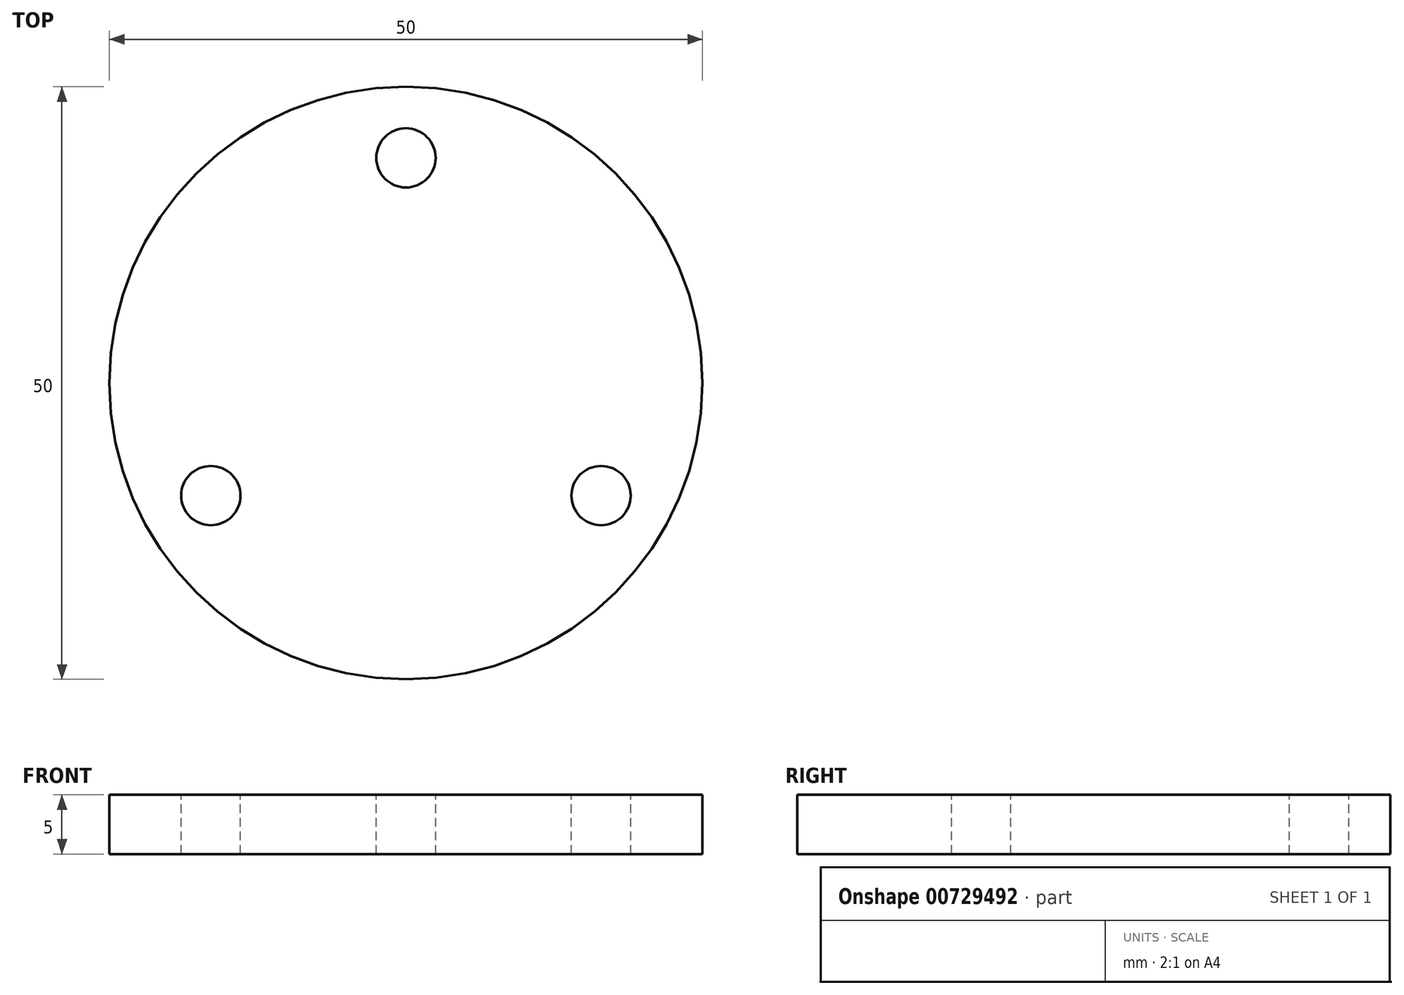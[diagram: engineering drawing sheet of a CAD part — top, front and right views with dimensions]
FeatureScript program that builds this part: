
annotation { "Feature Type Name" : "Feature", "Feature Type Description" : "" }
export const myFeature = defineFeature(function(context is Context, id is Id, definition is map)
    precondition{}
    {
        {
            var Q0;
            Q0=qCreatedBy(makeId("Top.planeOp"),FACE);
            var sketch = newSketch(context, id + "F0", { "sketchPlane" : qUnion([Q0])});
            skCircle(sketch, "E0", {"center": v(0, 0) * mm, "radius": 25 * mm});
            skCircle(sketch, "E1", {"center": v(0, 0) * mm, "radius": 7 * mm});
            skCircle(sketch, "E2", {"center": v(0, 19) * mm, "radius": 2.5 * mm});
            skCircle(sketch, "E3", {"center": v(-16.45, -9.5) * mm, "radius": 2.5 * mm});
            skCircle(sketch, "E4", {"center": v(16.45, -9.5) * mm, "radius": 2.5 * mm});
            skLineSegment(sketch, "E5", {"start": v(0, 0) * mm, "end": v(16.45, -9.5) * mm, "construction": true});
            skLineSegment(sketch, "E6", {"start": v(0, 0) * mm, "end": v(-16.45, -9.5) * mm, "construction": true});
            skLineSegment(sketch, "E7", {"start": v(0, 0) * mm, "end": v(0, 19) * mm, "construction": true});
            skSolve(sketch);
        }
        {
            var Q0;
            Q0=sQuery(id+"F0.wireOp",EDGE,"E4");
            var Q1;
            Q1=sQuery(id+"F0.wireOp",EDGE,"E3");
            var Q2;
            Q2=sQuery(id+"F0.wireOp",EDGE,"E2");
            var Q3;
            Q3=sQuery(id+"F0.wireOp",EDGE,"E0");
            extrude(context, id + "F1", {"bodyType" : ToolBodyType.SURFACE, "surfaceEntities" : qUnion([Q0, Q1, Q2, Q3]), "depth" : 5 * mm, "offsetDistance" : 25 * mm});
        }
    });
